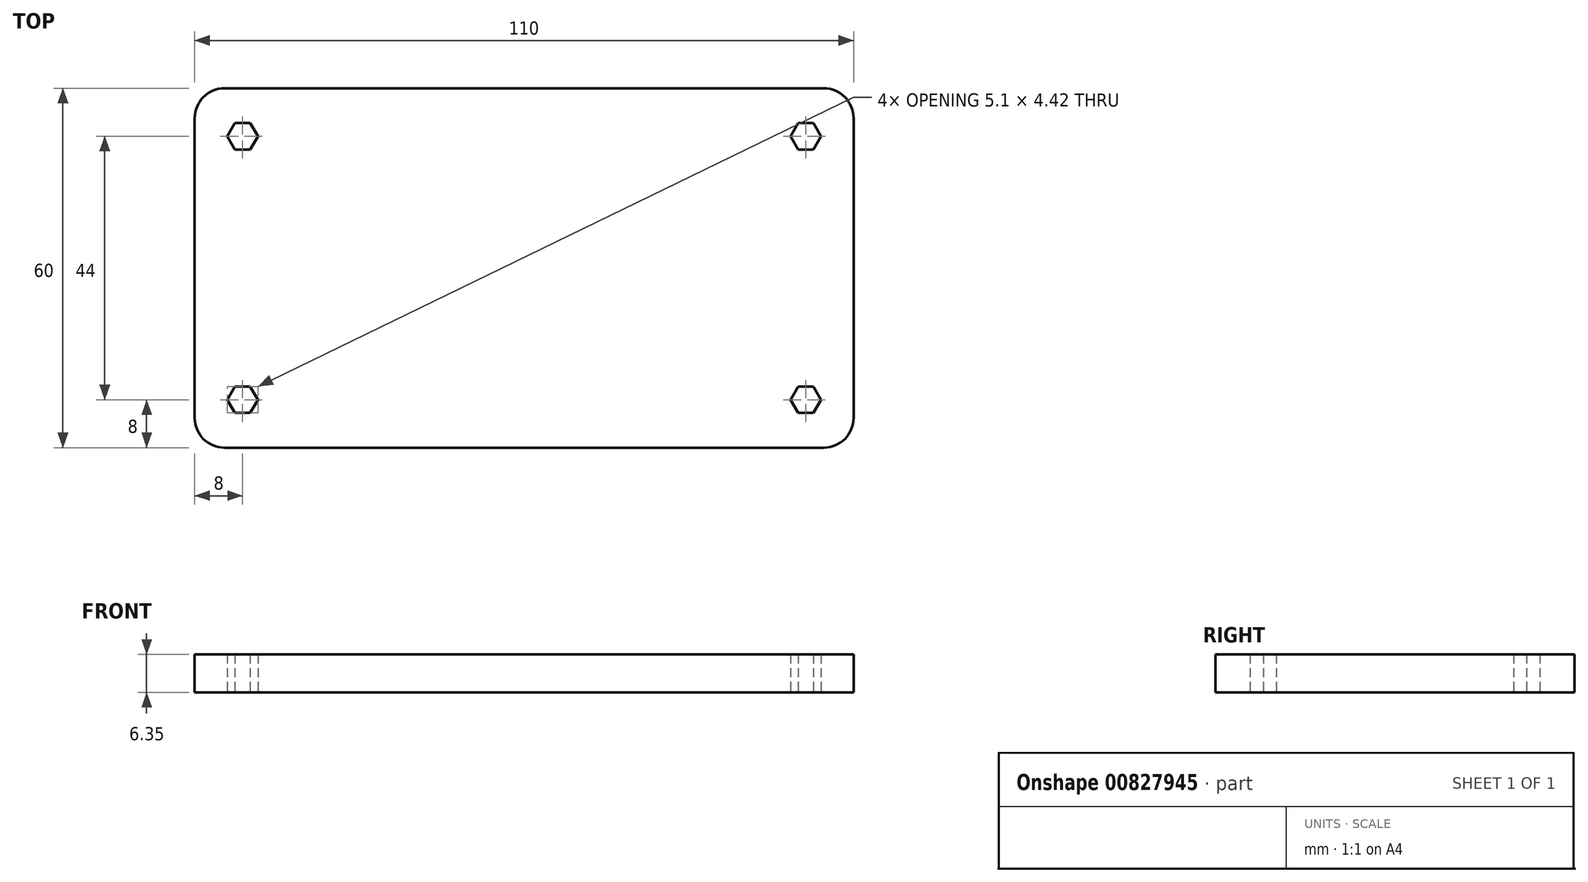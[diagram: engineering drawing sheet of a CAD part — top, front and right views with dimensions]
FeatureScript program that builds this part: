
annotation { "Feature Type Name" : "Feature", "Feature Type Description" : "" }
export const myFeature = defineFeature(function(context is Context, id is Id, definition is map)
    precondition{}
    {
        {
            var Q0;
            Q0=qCreatedBy(makeId("Top.planeOp"),FACE);
            var sketch = newSketch(context, id + "F0", { "sketchPlane" : qUnion([Q0])});
            skLineSegment(sketch, "E0.bottom", {"start": v(-55, 30) * mm, "end": v(55, 30) * mm});
            skLineSegment(sketch, "E0.top", {"start": v(-55, -30) * mm, "end": v(55, -30) * mm});
            skLineSegment(sketch, "E0.left", {"start": v(-55, 30) * mm, "end": v(-55, -30) * mm});
            skLineSegment(sketch, "E0.right", {"start": v(55, 30) * mm, "end": v(55, -30) * mm});
            skCircle(sketch, "E1.cCircle", {"center": v(-47, 22) * mm, "radius": 2.55 * mm, "construction": true});
            skLineSegment(sketch, "E1.0", {"start": v(-44.45, 22) * mm, "end": v(-45.73, 19.8) * mm});
            skLineSegment(sketch, "E1.1", {"start": v(-45.73, 19.8) * mm, "end": v(-48.27, 19.8) * mm});
            skLineSegment(sketch, "E1.2", {"start": v(-48.27, 19.8) * mm, "end": v(-49.55, 22) * mm});
            skLineSegment(sketch, "E1.3", {"start": v(-49.55, 22) * mm, "end": v(-48.28, 24.2) * mm});
            skLineSegment(sketch, "E1.4", {"start": v(-48.27, 24.2) * mm, "end": v(-45.72, 24.2) * mm});
            skLineSegment(sketch, "E1.5", {"start": v(-45.72, 24.2) * mm, "end": v(-44.45, 22) * mm});
            skCircle(sketch, "E2.cCircle", {"center": v(47, 22) * mm, "radius": 2.55 * mm, "construction": true});
            skLineSegment(sketch, "E2.0", {"start": v(44.45, 22) * mm, "end": v(45.73, 24.2) * mm});
            skLineSegment(sketch, "E2.1", {"start": v(45.73, 24.2) * mm, "end": v(48.27, 24.2) * mm});
            skLineSegment(sketch, "E2.2", {"start": v(48.27, 24.2) * mm, "end": v(49.55, 22) * mm});
            skLineSegment(sketch, "E2.3", {"start": v(49.55, 22) * mm, "end": v(48.27, 19.8) * mm});
            skLineSegment(sketch, "E2.4", {"start": v(48.28, 19.8) * mm, "end": v(45.73, 19.8) * mm});
            skLineSegment(sketch, "E2.5", {"start": v(45.73, 19.8) * mm, "end": v(44.45, 22) * mm});
            skCircle(sketch, "E3.cCircle", {"center": v(47, -22) * mm, "radius": 2.55 * mm, "construction": true});
            skLineSegment(sketch, "E3.0", {"start": v(44.45, -22) * mm, "end": v(45.72, -19.8) * mm});
            skLineSegment(sketch, "E3.1", {"start": v(45.72, -19.8) * mm, "end": v(48.27, -19.8) * mm});
            skLineSegment(sketch, "E3.2", {"start": v(48.28, -19.8) * mm, "end": v(49.55, -22) * mm});
            skLineSegment(sketch, "E3.3", {"start": v(49.55, -22) * mm, "end": v(48.27, -24.2) * mm});
            skLineSegment(sketch, "E3.4", {"start": v(48.27, -24.2) * mm, "end": v(45.73, -24.2) * mm});
            skLineSegment(sketch, "E3.5", {"start": v(45.73, -24.2) * mm, "end": v(44.45, -22) * mm});
            skCircle(sketch, "E4.cCircle", {"center": v(-47, -22) * mm, "radius": 2.55 * mm, "construction": true});
            skLineSegment(sketch, "E4.0", {"start": v(-44.45, -22) * mm, "end": v(-45.72, -24.2) * mm});
            skLineSegment(sketch, "E4.1", {"start": v(-45.72, -24.2) * mm, "end": v(-48.27, -24.2) * mm});
            skLineSegment(sketch, "E4.2", {"start": v(-48.27, -24.2) * mm, "end": v(-49.55, -22) * mm});
            skLineSegment(sketch, "E4.3", {"start": v(-49.55, -22) * mm, "end": v(-48.28, -19.8) * mm});
            skLineSegment(sketch, "E4.4", {"start": v(-48.28, -19.8) * mm, "end": v(-45.72, -19.8) * mm});
            skLineSegment(sketch, "E4.5", {"start": v(-45.72, -19.8) * mm, "end": v(-44.45, -22) * mm});
            skSolve(sketch);
        }
        {
            var Q0;
            Q0=makeQuery(id+"F0.imprint","IMPRINT",FACE,{"disambiguationData":[TD([[makeQuery(id+"F0.imprint","IMPRINT",EDGE,{"derivedFrom":sQuery(id+"F0.wireOp",EDGE,"E0.bottom")}),-1.0]])]});
            extrude(context, id + "F1", {"entities" : qUnion([Q0]), "depth" : 6.35 * mm, "offsetDistance" : 25 * mm});
        }
        {
            var Q0;
            Q0=makeQuery(id+"F1.opExtrude","SWEPT_EDGE",EDGE,{"disambiguationData":[OSD([sQuery(id+"F0.wireOp",EDGE,"E0.bottom"),sQuery(id+"F0.wireOp",EDGE,"E0.left")])]});
            var Q1;
            Q1=makeQuery(id+"F1.opExtrude","SWEPT_EDGE",EDGE,{"disambiguationData":[OSD([sQuery(id+"F0.wireOp",EDGE,"E0.top"),sQuery(id+"F0.wireOp",EDGE,"E0.left")])]});
            var Q2;
            Q2=makeQuery(id+"F1.opExtrude","SWEPT_EDGE",EDGE,{"disambiguationData":[OSD([sQuery(id+"F0.wireOp",EDGE,"E0.bottom"),sQuery(id+"F0.wireOp",EDGE,"E0.right")])]});
            var Q3;
            Q3=makeQuery(id+"F1.opExtrude","SWEPT_EDGE",EDGE,{"disambiguationData":[OSD([sQuery(id+"F0.wireOp",EDGE,"E0.top"),sQuery(id+"F0.wireOp",EDGE,"E0.right")])]});
            fillet(context, id + "F2", {"entities" : qUnion([Q0, Q1, Q2, Q3]), "radius" : 5 * mm, "tangentPropagation" : true, "allowEdgeOverflow" : false});
        }
    });
